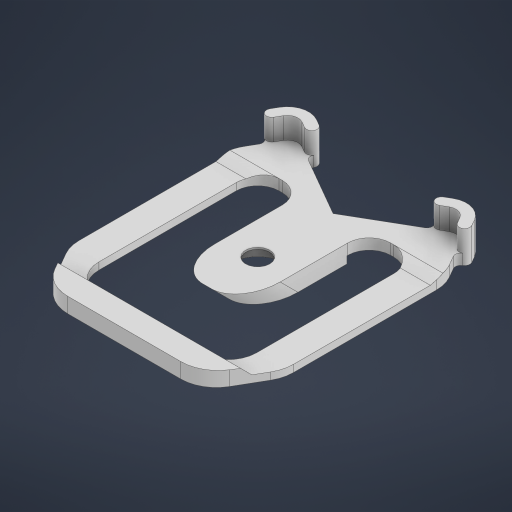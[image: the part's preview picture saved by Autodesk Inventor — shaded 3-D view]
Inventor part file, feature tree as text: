
AUTODESK INVENTOR PART (.ipt)
format: ipt  version: 2023 (Build 270158000, 158)  size: 450,560 bytes
history: native  units: in
note: dims shown in document units (in); Inventor stores cm internally (conversion verified against a paired STEP export)
features: extrude x7, chamfer x4, sketch x2, fillet x2, draft x1
ambient origin geometry x8: Origin, YZ Plane, XZ Plane, XY Plane, X Axis, Y Axis, Z Axis, Center Point
bodies: Solid1 (feature_tree)
feature tree (16):
  extrude  "Extrusion1"  Depth=0.1181in
  extrude  "Extrusion2"  Depth=0.1969in TaperAngle=0.0deg
  extrude  "Extrusion3"  Depth=0.0197in
  extrude  "Extrusion4"  Depth=0.1181in
  extrude  "Extrusion5"  Depth=0.315in
  chamfer  "Chamfer1"  Distance=0.2362in
  chamfer  "Chamfer2"  Distance=0.2362in
  chamfer  "Chamfer3"  Distance=0.5689in
  sketch  "Sketch2"  dims[d1=0.374in d3=120.0deg d4=60.0deg d5=0.1772in d6=2.9528in d11=0.0886in d14=60.0deg d15=0.1772in d16=0.0886in d17=1.5748in d18=0.1181in]
  fillet  "Fillet3"  Radius=0.0787in
  extrude  "Extrusion7"  Depth=0.0787in
  draft  "FaceDraft3"
  fillet  "Fillet10"  Radius=0.0787in
  chamfer  "Chamfer8"  Distance=0.0197in
  extrude  "Extrusion10"  Depth=0.0394in TaperAngle=0.0deg
  sketch  "Sketch7"  dims[d19=0.3937in d20=0.1969in d21=0.0in d22=0.2657in d24=0.1181in d25=0.315in d26=0.2362in d27=0.2362in d28=0.5689in d29=0.0787in d30=0.0787in d31=0.0787in d32=0.0197in d33=0.0in d34=0.0394in d35=0.0in d36=0.2362in d37=0.0in d38=0.0in d39=0.0in d40=0.0in d41=0.0in d42=0.0591in d43=0.2362in d44=0.0in d45=0.2756in d46=0.0492in d47=0.0in d48=0.2756in d49=0.0098in d50=45.0deg d52=0.0394in d53=0.1575in d54=75.0deg d55=0.0394in d56=0.1575in d57=75.0deg d66=0.315in d67=0.3937in d72=0.1575in d73=0.0in d74=45.0deg d105=0.315in d106=0.0787in d107=0.0787in d108=0.2405in d109=0.0787in d110=0.0in d51=0.0in d59=0.0in d60=0.0in d61=0.0in d62=0.0in d63=0.0in d64=0.0in d65=0.0in d68=0.0344in d69=0.0197in d70=0.0344in d104=0.0in]
